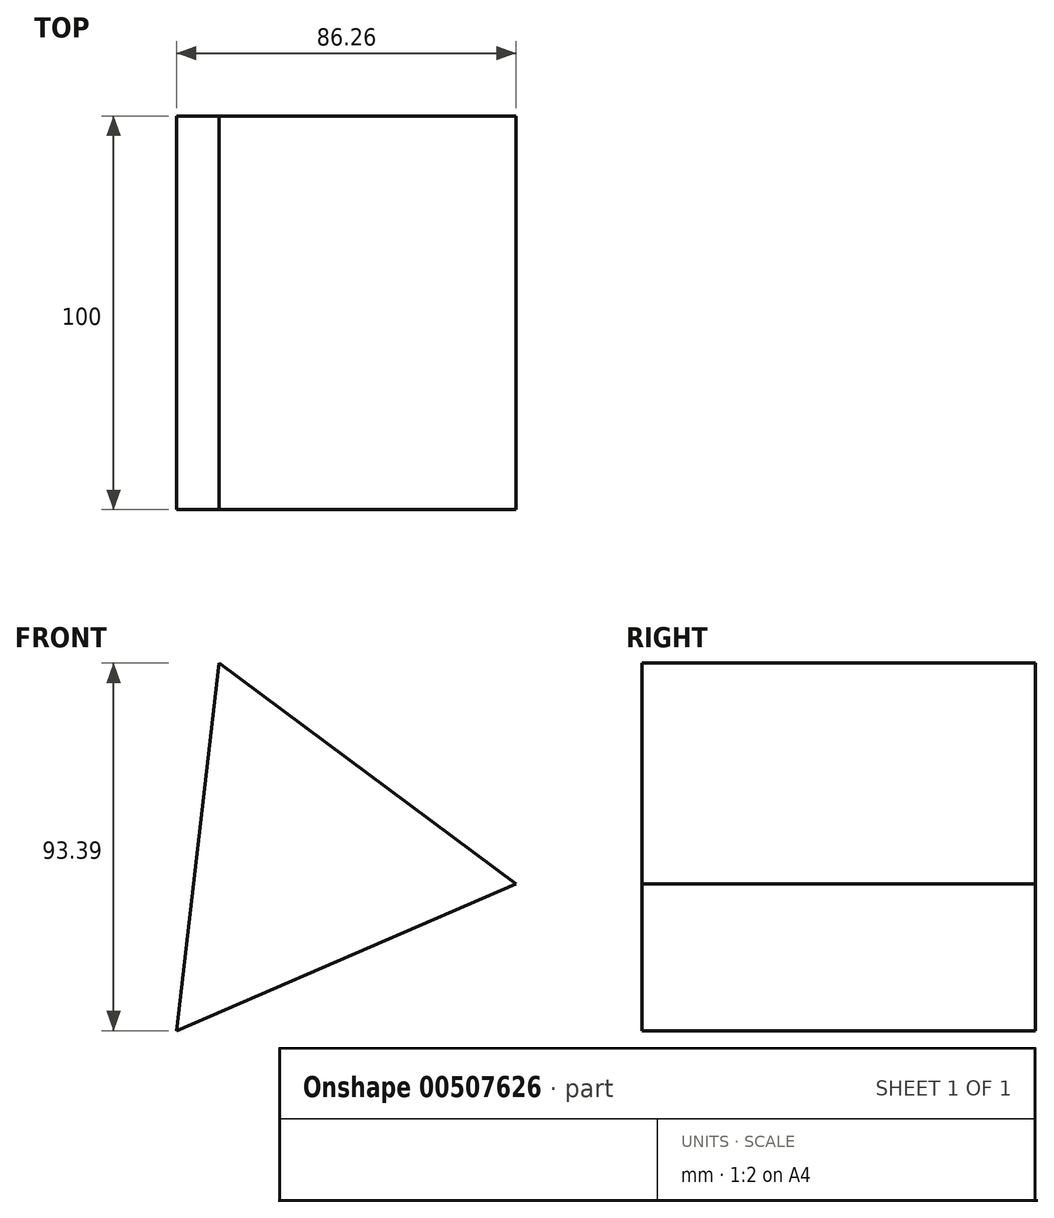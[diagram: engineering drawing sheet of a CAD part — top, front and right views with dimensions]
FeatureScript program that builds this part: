
annotation { "Feature Type Name" : "Feature", "Feature Type Description" : "" }
export const myFeature = defineFeature(function(context is Context, id is Id, definition is map)
    precondition{}
    {
        {
            var Q0;
            Q0=qCreatedBy(makeId("Front.planeOp"),FACE);
            var sketch = newSketch(context, id + "F0", { "sketchPlane" : qUnion([Q0])});
            skCircle(sketch, "E0.cCircle", {"center": v(0, 0) * mm, "radius": 54.27 * mm, "construction": true});
            skLineSegment(sketch, "E0.0", {"start": v(-32.35, -43.58) * mm, "end": v(-21.56, 49.8) * mm});
            skLineSegment(sketch, "E0.1", {"start": v(-21.56, 49.8) * mm, "end": v(53.91, -6.23) * mm});
            skLineSegment(sketch, "E0.2", {"start": v(53.91, -6.23) * mm, "end": v(-32.35, -43.58) * mm});
            skSolve(sketch);
        }
        {
            var Q0;
            Q0=makeQuery(id+"F0.imprint","IMPRINT",FACE,{"disambiguationData":[TD([[makeQuery(id+"F0.imprint","IMPRINT",EDGE,{"derivedFrom":sQuery(id+"F0.wireOp",EDGE,"E0.0")}),-1.0]])]});
            extrude(context, id + "F1", {"entities" : qUnion([Q0]), "endBound" : BoundingType.SYMMETRIC, "depth" : 100 * mm});
        }
    });
